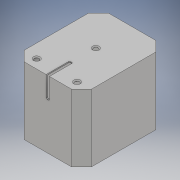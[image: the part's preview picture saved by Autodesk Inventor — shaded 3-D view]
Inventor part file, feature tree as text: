
AUTODESK INVENTOR PART (.ipt)
format: ipt  version: 2017 (Build 210142000, 142)  size: 450,048 bytes
history: native  units: mm
features: extrude x5, other x3, sketch x3, fillet x3, hole x3
ambient origin geometry x8: Origin, YZ Plane, XZ Plane, XY Plane, X Axis, Y Axis, Z Axis, Center Point
bodies: Body1 (feature_tree)
feature tree (17):
  other  "Твердое тело1"
  sketch  "Эскиз1"
  extrude  "Выдавливание1"  Depth=58.6mm
  extrude  "Выдавливание2"  Depth=74.0mm
  fillet  "Сопряжение1"  Radius=8.5mm
  extrude  "Выдавливание3"  Depth=8.5mm
  extrude  "Выдавливание4"  Depth=8.5mm
  extrude  "Выдавливание5"  Depth=8.5mm
  other  "Комбинировать1"
  hole  "Отверстие4"  [1 undecoded]
  hole  "Отверстие5"  [1 undecoded]
  hole  "Отверстие6"  [1 undecoded]
  fillet  "Сопряжение2"  Radius=8.5mm
  fillet  "Сопряжение3"  Radius=1.2mm
  other  "Твердое тело2"
  sketch  "Эскиз2"
  sketch  "Эскиз3"
note: 3 required parameter values undecoded (feature->parameter linkage not recoverable at this tier; creation-order binding heuristic only, values carry confidence <= 0.55)
